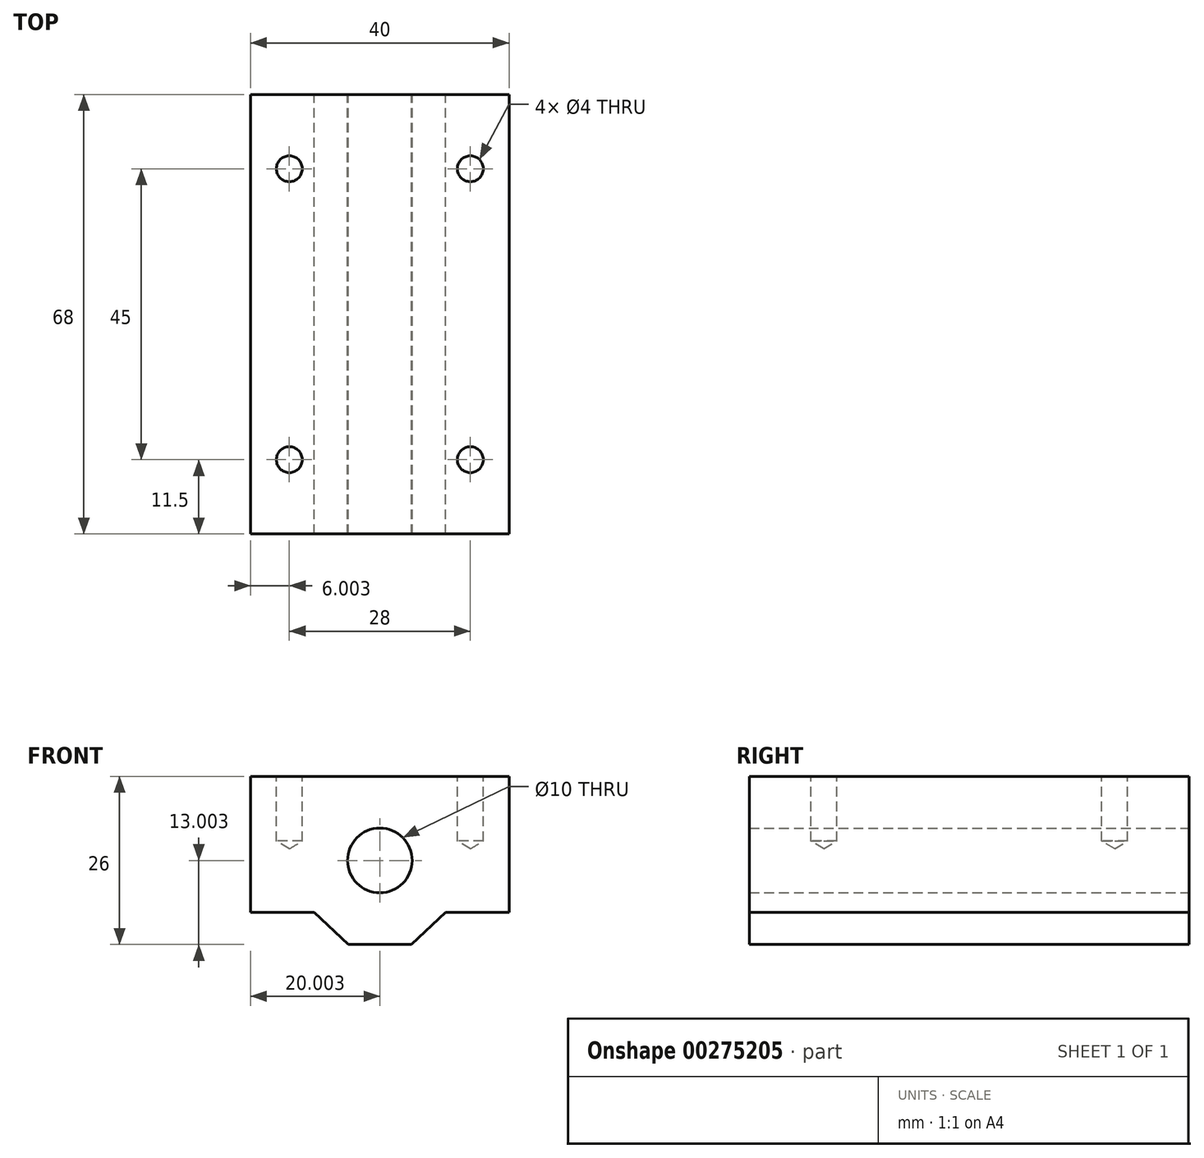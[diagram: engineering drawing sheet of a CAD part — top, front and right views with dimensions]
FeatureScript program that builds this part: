
annotation { "Feature Type Name" : "Feature", "Feature Type Description" : "" }
export const myFeature = defineFeature(function(context is Context, id is Id, definition is map)
    precondition{}
    {
        {
            var Q0;
            Q0=qCreatedBy(makeId("Front.planeOp"),FACE);
            var sketch = newSketch(context, id + "F0", { "sketchPlane" : qUnion([Q0])});
            skLineSegment(sketch, "E0.bottom", {"start": v(-37.72, 34.14) * mm, "end": v(2.28, 34.14) * mm});
            skLineSegment(sketch, "E0.top", {"start": v(-22.59, 8.14) * mm, "end": v(-12.85, 8.14) * mm});
            skLineSegment(sketch, "E0.left", {"start": v(-37.72, 34.14) * mm, "end": v(-37.72, 13.14) * mm});
            skLineSegment(sketch, "E0.right", {"start": v(2.28, 34.14) * mm, "end": v(2.28, 13.14) * mm});
            skLineSegment(sketch, "E1", {"start": v(-17.72, 34.14) * mm, "end": v(-17.72, 8.14) * mm, "construction": true});
            skLineSegment(sketch, "E2", {"start": v(-37.72, 21.14) * mm, "end": v(2.28, 21.14) * mm, "construction": true});
            skCircle(sketch, "E3", {"center": v(-17.72, 21.14) * mm, "radius": 5 * mm});
            skLineSegment(sketch, "E4", {"start": v(2.28, 13.14) * mm, "end": v(-7.55, 13.14) * mm});
            skLineSegment(sketch, "E5", {"start": v(-7.55, 13.14) * mm, "end": v(-12.85, 8.14) * mm});
            skLineSegment(sketch, "E6", {"start": v(-37.72, 13.14) * mm, "end": v(-27.89, 13.14) * mm});
            skLineSegment(sketch, "E7", {"start": v(-27.89, 13.14) * mm, "end": v(-22.59, 8.14) * mm});
            skPoint(sketch, "E8.orphan", {"position": v(2.28, 8.14) * mm});
            skPoint(sketch, "E9.orphan", {"position": v(-37.72, 8.14) * mm});
            skSolve(sketch);
        }
        {
            var Q0;
            Q0=makeQuery(id+"F0.imprint","IMPRINT",FACE,{"disambiguationData":[TD([[makeQuery(id+"F0.imprint","IMPRINT",EDGE,{"derivedFrom":sQuery(id+"F0.wireOp",EDGE,"E0.bottom")}),-1.0]])]});
            extrude(context, id + "F1", {"entities" : qUnion([Q0]), "depth" : 68 * mm});
        }
        {
            var Q0;
            Q0=makeQuery(id+"F1.opExtrude","SWEPT_FACE",FACE,{"disambiguationData":[OSD([sQuery(id+"F0.wireOp",EDGE,"E0.bottom")])]});
            var sketch = newSketch(context, id + "F2", { "sketchPlane" : qUnion([Q0])});
            skLineSegment(sketch, "E10", {"start": v(-17.72, 0) * mm, "end": v(-17.72, -68) * mm, "construction": true});
            skLineSegment(sketch, "E11", {"start": v(-31.72, 0) * mm, "end": v(-31.72, -68) * mm});
            skLineSegment(sketch, "E12", {"start": v(-3.72, 0) * mm, "end": v(-3.72, -68) * mm});
            skLineSegment(sketch, "E13", {"start": v(-37.72, -34) * mm, "end": v(2.28, -34) * mm, "construction": true});
            skLineSegment(sketch, "E14", {"start": v(-37.72, -11.5) * mm, "end": v(2.28, -11.5) * mm});
            skLineSegment(sketch, "E15", {"start": v(-37.72, -56.5) * mm, "end": v(2.28, -56.5) * mm});
            skPoint(sketch, "E16", {"position": v(-31.72, -11.5) * mm});
            skPoint(sketch, "E17", {"position": v(-3.72, -11.5) * mm});
            skPoint(sketch, "E18", {"position": v(-31.72, -56.5) * mm});
            skPoint(sketch, "E19", {"position": v(-3.72, -56.5) * mm});
            skSolve(sketch);
        }
        {
            var Q0;
            Q0=sQuery(id+"F2.wireOp",VERTEX,"E16");
            var Q1;
            Q1=sQuery(id+"F2.wireOp",VERTEX,"E18");
            var Q2;
            Q2=sQuery(id+"F2.wireOp",VERTEX,"E17");
            var Q3;
            Q3=sQuery(id+"F2.wireOp",VERTEX,"E19");
            var Q4;
            Q4=makeQuery(id+"F1.opExtrude","SWEPT_BODY",BODY,{"disambiguationData":[OSD([sQuery(id+"F0.wireOp",EDGE,"E0.bottom"),sQuery(id+"F0.wireOp",EDGE,"E0.top"),sQuery(id+"F0.wireOp",EDGE,"E0.left"),sQuery(id+"F0.wireOp",EDGE,"E0.right"),sQuery(id+"F0.wireOp",EDGE,"ug5t7xEK-u7xN-v8Ie-mRre-GjczhrxJ6Di6")])]});
            hole(context, id + "F3", {"style" : HoleStyle.SIMPLE, "endStyle" : HoleEndStyle.BLIND, "holeDiameter" : 4 * mm, "holeDepth" : 10 * mm, "tappedDepth" : 12 * mm, "tapClearance" : 3, "locations" : qUnion([Q0, Q1, Q2, Q3]), "scope" : qUnion([Q4])});
        }
    });
